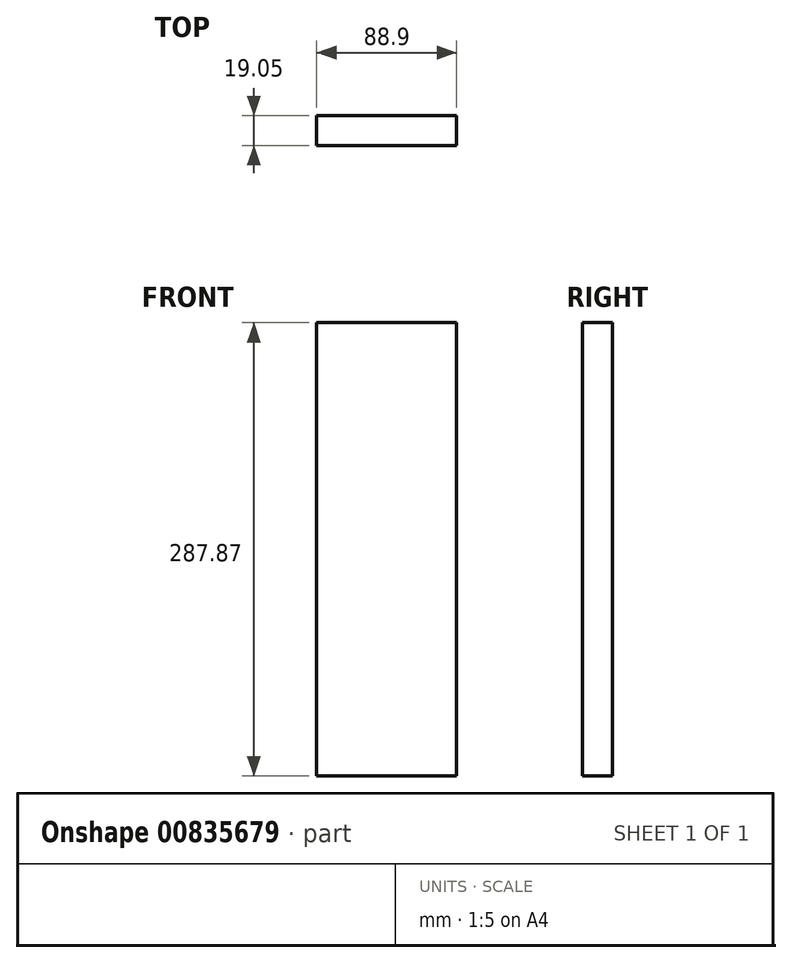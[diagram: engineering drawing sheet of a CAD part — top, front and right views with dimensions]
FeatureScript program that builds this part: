
annotation { "Feature Type Name" : "Feature", "Feature Type Description" : "" }
export const myFeature = defineFeature(function(context is Context, id is Id, definition is map)
    precondition{}
    {
        {
            var Q0;
            Q0=qCreatedBy(makeId("Front.planeOp"),FACE);
            var sketch = newSketch(context, id + "F0", { "sketchPlane" : qUnion([Q0])});
            skLineSegment(sketch, "E0.bottom", {"start": v(0, 0) * mm, "end": v(88.9, 0) * mm});
            skLineSegment(sketch, "E0.top", {"start": v(0, 287.87) * mm, "end": v(88.9, 287.87) * mm});
            skLineSegment(sketch, "E0.left", {"start": v(0, 0) * mm, "end": v(0, 287.87) * mm});
            skLineSegment(sketch, "E0.right", {"start": v(88.9, 0) * mm, "end": v(88.9, 287.87) * mm});
            skSolve(sketch);
        }
        {
            var Q0;
            Q0=qSketchRegion(id+"F0",true);
            extrude(context, id + "F1", {"entities" : qUnion([Q0]), "depth" : 19.05 * mm, "offsetDistance" : 25.4 * mm});
        }
    });
